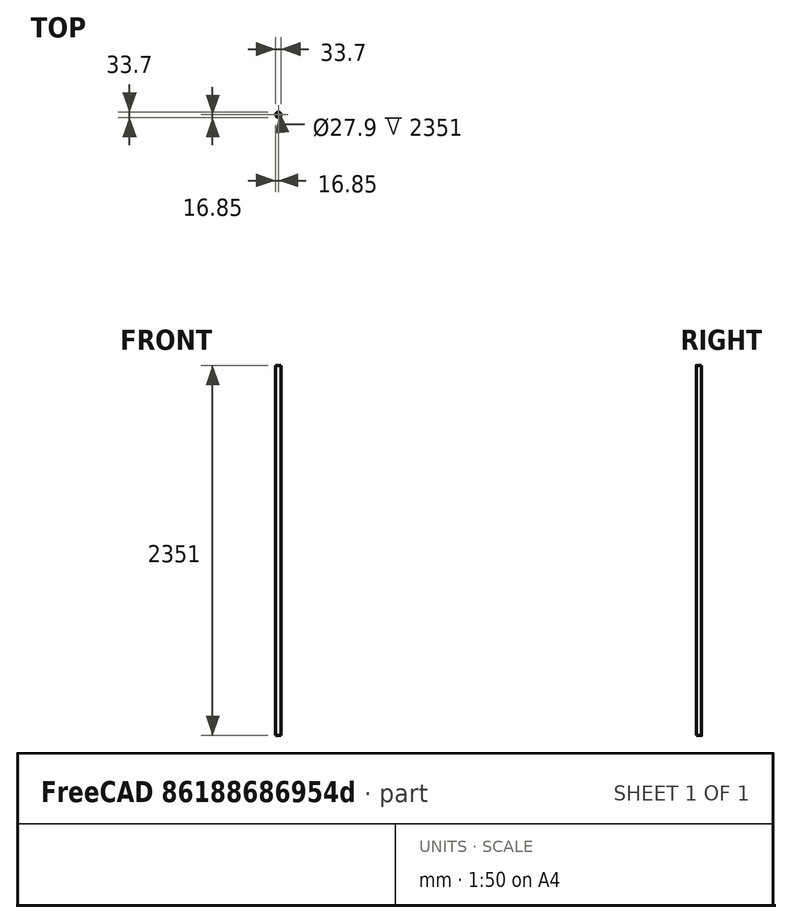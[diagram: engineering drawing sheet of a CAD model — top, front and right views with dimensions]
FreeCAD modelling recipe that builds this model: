
FCSTD DOCUMENT  (FreeCAD 0.18R4 (GitTag))
Label: door-rod
License: All rights reserved
LicenseURL: http://en.wikipedia.org/wiki/All_rights_reserved
objects: Sketcher::SketchObject×1, PartDesign::Pad×1, PartDesign::Body×1
note: 4 computed .brp shape members not serialized (recipe doc carries the construction recipe); baked Part::Feature solids carry a one-line shape summary decoded from their .brp

FEATURE [Sketcher::SketchObject] Sketch
  MapMode = 5
  Support = -> [XY_Plane]
  sketch-geometry (2):
    g0: Circle CenterX=0 CenterY=0 CenterZ=0 NormalX=0 NormalY=0 NormalZ=1 AngleXU=0 Radius=13.95
    g1: Circle CenterX=0 CenterY=0 CenterZ=0 NormalX=0 NormalY=0 NormalZ=1 AngleXU=0 Radius=16.85
  constraints (4):
    c: Coincident(g0,g-1)
    c: Coincident(g1,g0)
    c: Diameter(g0) = 27.9
    c: Diameter(g1) = 33.7
FEATURE [PartDesign::Pad] Pad
  Length = 2351
  Length2 = 100
  Profile = -> Sketch
  Refine = true
  Type = 0
FEATURE [PartDesign::Body] Body
  Group = -> [Sketch,Pad]
  Origin = -> Origin
  Tip = -> Pad
